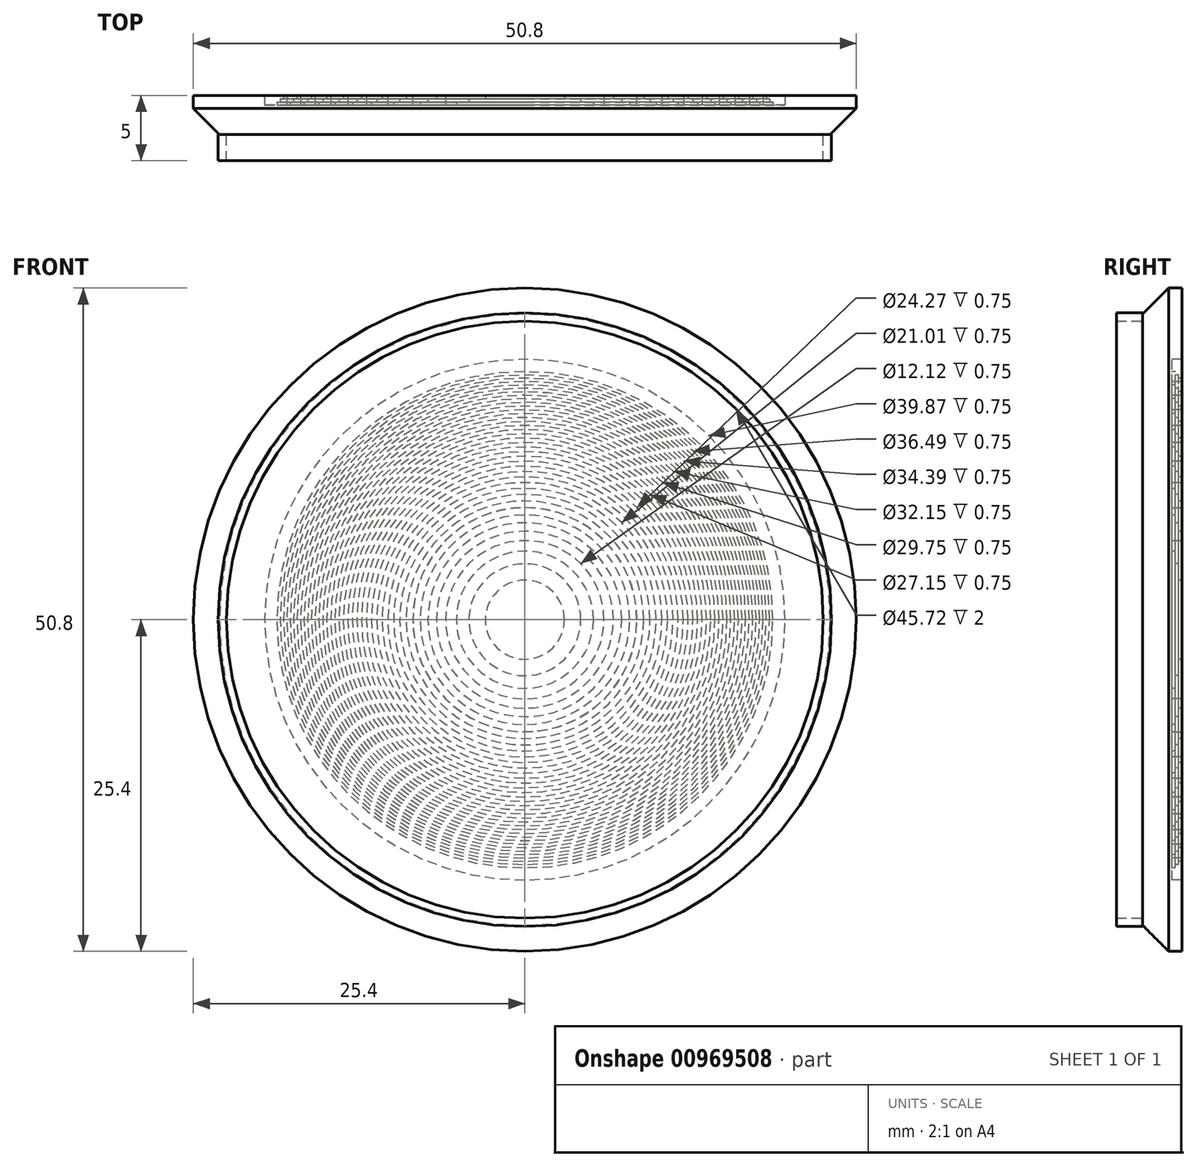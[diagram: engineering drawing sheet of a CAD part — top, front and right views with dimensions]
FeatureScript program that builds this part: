
annotation { "Feature Type Name" : "Feature", "Feature Type Description" : "" }
export const myFeature = defineFeature(function(context is Context, id is Id, definition is map)
    precondition{}
    {
        {
            var Q0;
            Q0=qCreatedBy(makeId("Top.planeOp"),FACE);
            var sketch = newSketch(context, id + "F0", { "sketchPlane" : qUnion([Q0])});
            skLineSegment(sketch, "E0", {"start": v(0, 0) * mm, "end": v(25.4, 0) * mm});
            skLineSegment(sketch, "E1", {"start": v(0, 0) * mm, "end": v(0, 3) * mm});
            skLineSegment(sketch, "E2", {"start": v(3.03, 2.75) * mm, "end": v(3.03, 3) * mm});
            skLineSegment(sketch, "E3", {"start": v(0, 3) * mm, "end": v(3.03, 3) * mm});
            skLineSegment(sketch, "E4", {"start": v(4.28, 2.5) * mm, "end": v(4.28, 2.75) * mm});
            skLineSegment(sketch, "E5", {"start": v(4.28, 2.75) * mm, "end": v(3.03, 2.75) * mm});
            skLineSegment(sketch, "E6", {"start": v(5.25, 2.25) * mm, "end": v(5.25, 2.5) * mm});
            skLineSegment(sketch, "E7", {"start": v(5.25, 2.5) * mm, "end": v(4.28, 2.5) * mm});
            skLineSegment(sketch, "E8", {"start": v(6.06, 2.25) * mm, "end": v(5.25, 2.25) * mm});
            skLineSegment(sketch, "E9", {"start": v(6.06, 3) * mm, "end": v(6.06, 2.25) * mm});
            skLineSegment(sketch, "E10", {"start": v(7.42, 2.75) * mm, "end": v(6.78, 2.75) * mm});
            skLineSegment(sketch, "E11", {"start": v(8.02, 2.5) * mm, "end": v(7.42, 2.5) * mm});
            skLineSegment(sketch, "E12", {"start": v(8.57, 2.25) * mm, "end": v(8.02, 2.25) * mm});
            skLineSegment(sketch, "E13", {"start": v(6.78, 2.75) * mm, "end": v(6.78, 3) * mm});
            skLineSegment(sketch, "E14", {"start": v(6.78, 3) * mm, "end": v(6.06, 3) * mm});
            skLineSegment(sketch, "E15", {"start": v(7.42, 2.75) * mm, "end": v(7.42, 2.5) * mm});
            skLineSegment(sketch, "E16", {"start": v(8.02, 2.25) * mm, "end": v(8.02, 2.5) * mm});
            skLineSegment(sketch, "E17", {"start": v(9.1, 2.75) * mm, "end": v(9.1, 3) * mm});
            skLineSegment(sketch, "E18", {"start": v(9.1, 3) * mm, "end": v(8.58, 3) * mm});
            skLineSegment(sketch, "E19", {"start": v(8.57, 2.25) * mm, "end": v(8.58, 3) * mm});
            skLineSegment(sketch, "E20", {"start": v(9.59, 2.5) * mm, "end": v(9.59, 2.75) * mm});
            skLineSegment(sketch, "E21", {"start": v(9.59, 2.75) * mm, "end": v(9.1, 2.75) * mm});
            skLineSegment(sketch, "E22", {"start": v(10.06, 2.25) * mm, "end": v(10.06, 2.5) * mm});
            skLineSegment(sketch, "E23", {"start": v(10.06, 2.5) * mm, "end": v(9.59, 2.5) * mm});
            skLineSegment(sketch, "E24", {"start": v(10.5, 2.25) * mm, "end": v(10.06, 2.25) * mm});
            skLineSegment(sketch, "E25", {"start": v(10.5, 2.25) * mm, "end": v(10.5, 3) * mm});
            skLineSegment(sketch, "E26", {"start": v(10.94, 2.75) * mm, "end": v(10.94, 3) * mm});
            skLineSegment(sketch, "E27", {"start": v(10.94, 3) * mm, "end": v(10.5, 3) * mm});
            skLineSegment(sketch, "E28", {"start": v(11.35, 2.5) * mm, "end": v(11.35, 2.75) * mm});
            skLineSegment(sketch, "E29", {"start": v(11.35, 2.75) * mm, "end": v(10.94, 2.75) * mm});
            skLineSegment(sketch, "E30", {"start": v(11.75, 2.25) * mm, "end": v(11.75, 2.5) * mm});
            skLineSegment(sketch, "E31", {"start": v(11.75, 2.5) * mm, "end": v(11.35, 2.5) * mm});
            skLineSegment(sketch, "E32", {"start": v(12.14, 2.25) * mm, "end": v(11.75, 2.25) * mm});
            skLineSegment(sketch, "E33", {"start": v(12.51, 2.75) * mm, "end": v(12.51, 3) * mm});
            skLineSegment(sketch, "E34", {"start": v(12.88, 2.5) * mm, "end": v(12.88, 2.75) * mm});
            skLineSegment(sketch, "E35", {"start": v(12.88, 2.75) * mm, "end": v(12.51, 2.75) * mm});
            skLineSegment(sketch, "E36", {"start": v(12.14, 2.25) * mm, "end": v(12.14, 3) * mm});
            skLineSegment(sketch, "E37", {"start": v(12.14, 3) * mm, "end": v(12.51, 3) * mm});
            skLineSegment(sketch, "E38", {"start": v(13.23, 2.5) * mm, "end": v(12.88, 2.5) * mm});
            skLineSegment(sketch, "E39", {"start": v(13.58, 2.25) * mm, "end": v(13.23, 2.25) * mm});
            skLineSegment(sketch, "E40", {"start": v(13.23, 2.25) * mm, "end": v(13.23, 2.5) * mm});
            skLineSegment(sketch, "E41", {"start": v(13.58, 2.25) * mm, "end": v(13.58, 3) * mm});
            skLineSegment(sketch, "E42", {"start": v(13.91, 2.75) * mm, "end": v(13.91, 3) * mm});
            skLineSegment(sketch, "E43", {"start": v(13.91, 3) * mm, "end": v(13.58, 3) * mm});
            skLineSegment(sketch, "E44", {"start": v(14.24, 2.5) * mm, "end": v(14.24, 2.75) * mm});
            skLineSegment(sketch, "E45", {"start": v(14.24, 2.75) * mm, "end": v(13.91, 2.75) * mm});
            skLineSegment(sketch, "E46", {"start": v(14.56, 2.25) * mm, "end": v(14.56, 2.5) * mm});
            skLineSegment(sketch, "E47", {"start": v(14.56, 2.5) * mm, "end": v(14.24, 2.5) * mm});
            skLineSegment(sketch, "E48", {"start": v(14.88, 2.25) * mm, "end": v(14.56, 2.25) * mm});
            skLineSegment(sketch, "E49", {"start": v(15.19, 2.75) * mm, "end": v(15.19, 3) * mm});
            skLineSegment(sketch, "E50", {"start": v(14.88, 2.25) * mm, "end": v(14.88, 3) * mm});
            skLineSegment(sketch, "E51", {"start": v(14.88, 3) * mm, "end": v(15.19, 3) * mm});
            skLineSegment(sketch, "E52", {"start": v(15.49, 2.5) * mm, "end": v(15.49, 2.75) * mm});
            skLineSegment(sketch, "E53", {"start": v(15.49, 2.75) * mm, "end": v(15.19, 2.75) * mm});
            skLineSegment(sketch, "E54", {"start": v(15.79, 2.25) * mm, "end": v(15.79, 2.5) * mm});
            skLineSegment(sketch, "E55", {"start": v(15.79, 2.5) * mm, "end": v(15.49, 2.5) * mm});
            skLineSegment(sketch, "E56", {"start": v(16.08, 2.25) * mm, "end": v(15.79, 2.25) * mm});
            skLineSegment(sketch, "E57", {"start": v(16.08, 2.25) * mm, "end": v(16.08, 3) * mm});
            skLineSegment(sketch, "E58", {"start": v(16.36, 2.75) * mm, "end": v(16.36, 3) * mm});
            skLineSegment(sketch, "E59", {"start": v(16.36, 3) * mm, "end": v(16.08, 3) * mm});
            skLineSegment(sketch, "E60", {"start": v(16.64, 2.5) * mm, "end": v(16.64, 2.75) * mm});
            skLineSegment(sketch, "E61", {"start": v(16.64, 2.75) * mm, "end": v(16.36, 2.75) * mm});
            skLineSegment(sketch, "E62", {"start": v(16.92, 2.25) * mm, "end": v(16.92, 2.5) * mm});
            skLineSegment(sketch, "E63", {"start": v(16.92, 2.5) * mm, "end": v(16.64, 2.5) * mm});
            skLineSegment(sketch, "E64", {"start": v(17.2, 2.25) * mm, "end": v(16.92, 2.25) * mm});
            skLineSegment(sketch, "E65", {"start": v(17.46, 2.75) * mm, "end": v(17.46, 3) * mm});
            skLineSegment(sketch, "E66", {"start": v(17.73, 2.5) * mm, "end": v(17.73, 2.75) * mm});
            skLineSegment(sketch, "E67", {"start": v(17.99, 2.25) * mm, "end": v(17.99, 2.5) * mm});
            skLineSegment(sketch, "E68", {"start": v(17.99, 2.5) * mm, "end": v(17.73, 2.5) * mm});
            skLineSegment(sketch, "E69", {"start": v(17.73, 2.75) * mm, "end": v(17.46, 2.75) * mm});
            skLineSegment(sketch, "E70", {"start": v(17.2, 2.25) * mm, "end": v(17.2, 3) * mm});
            skLineSegment(sketch, "E71", {"start": v(17.2, 3) * mm, "end": v(17.46, 3) * mm});
            skLineSegment(sketch, "E72", {"start": v(18.25, 2.25) * mm, "end": v(17.99, 2.25) * mm});
            skLineSegment(sketch, "E73", {"start": v(18.25, 2.25) * mm, "end": v(18.25, 3) * mm});
            skLineSegment(sketch, "E74", {"start": v(18.5, 2.75) * mm, "end": v(18.5, 3) * mm});
            skLineSegment(sketch, "E75", {"start": v(18.5, 3) * mm, "end": v(18.25, 3) * mm});
            skLineSegment(sketch, "E76", {"start": v(18.75, 2.5) * mm, "end": v(18.75, 2.75) * mm});
            skLineSegment(sketch, "E77", {"start": v(18.75, 2.75) * mm, "end": v(18.5, 2.75) * mm});
            skLineSegment(sketch, "E78", {"start": v(19, 2.25) * mm, "end": v(19, 2.5) * mm});
            skLineSegment(sketch, "E79", {"start": v(19, 2.5) * mm, "end": v(18.75, 2.5) * mm});
            skLineSegment(sketch, "E80", {"start": v(25.4, 0) * mm, "end": v(25.4, 3) * mm});
            skLineSegment(sketch, "E81", {"start": v(25.4, 3) * mm, "end": v(19.94, 3) * mm});
            skLineSegment(sketch, "E82", {"start": v(19.94, 3) * mm, "end": v(19.94, 2.25) * mm});
            skLineSegment(sketch, "E83", {"start": v(19.94, 2.25) * mm, "end": v(19, 2.25) * mm});
            skSolve(sketch);
        }
        {
            var Q0;
            Q0=makeQuery(id+"F0.imprint","IMPRINT",FACE,{"disambiguationData":[TD([[makeQuery(id+"F0.imprint","IMPRINT",EDGE,{"derivedFrom":sQuery(id+"F0.wireOp",EDGE,"E0")}),1.0]])]});
            var Q1;
            Q1=sQuery(id+"F0.wireOp",EDGE,"E1");
            revolve(context, id + "F1", {"surfaceOperationType" : NewSurfaceOperationType.NEW, "entities" : qUnion([Q0]), "axis" : qUnion([Q1]), "revolveType" : RevolveType.FULL});
        }
        {
            var Q0;
            Q0=makeQuery(id+"F1.opRevolve","SWEPT_EDGE",EDGE,{"disambiguationData":[OSD([sQuery(id+"F0.wireOp",EDGE,"E0"),sQuery(id+"F0.wireOp",EDGE,"E80")])]});
            chamfer(context, id + "F2", {"entities" : qUnion([Q0]), "width" : 2 * mm, "tangentPropagation" : true});
        }
        {
            var Q0;
            Q0=qCreatedBy(makeId("Front.planeOp"),FACE);
            var sketch = newSketch(context, id + "F3", { "sketchPlane" : qUnion([Q0])});
            skCircle(sketch, "E84", {"center": v(0, 0) * mm, "radius": 23.5 * mm});
            skCircle(sketch, "E85", {"center": v(0, 0) * mm, "radius": 22.86 * mm});
            skSolve(sketch);
        }
        {
            var Q0;
            Q0=makeQuery(id+"F3.imprint","IMPRINT",FACE,{"disambiguationData":[TD([[makeQuery(id+"F3.imprint","IMPRINT",EDGE,{"derivedFrom":sQuery(id+"F3.wireOp",EDGE,"E84")}),1.0]])]});
            extrude(context, id + "F4", {"entities" : qUnion([Q0]), "operationType" : NewBodyOperationType.ADD, "depth" : 2 * mm, "offsetDistance" : 25.4 * mm});
        }
    });
